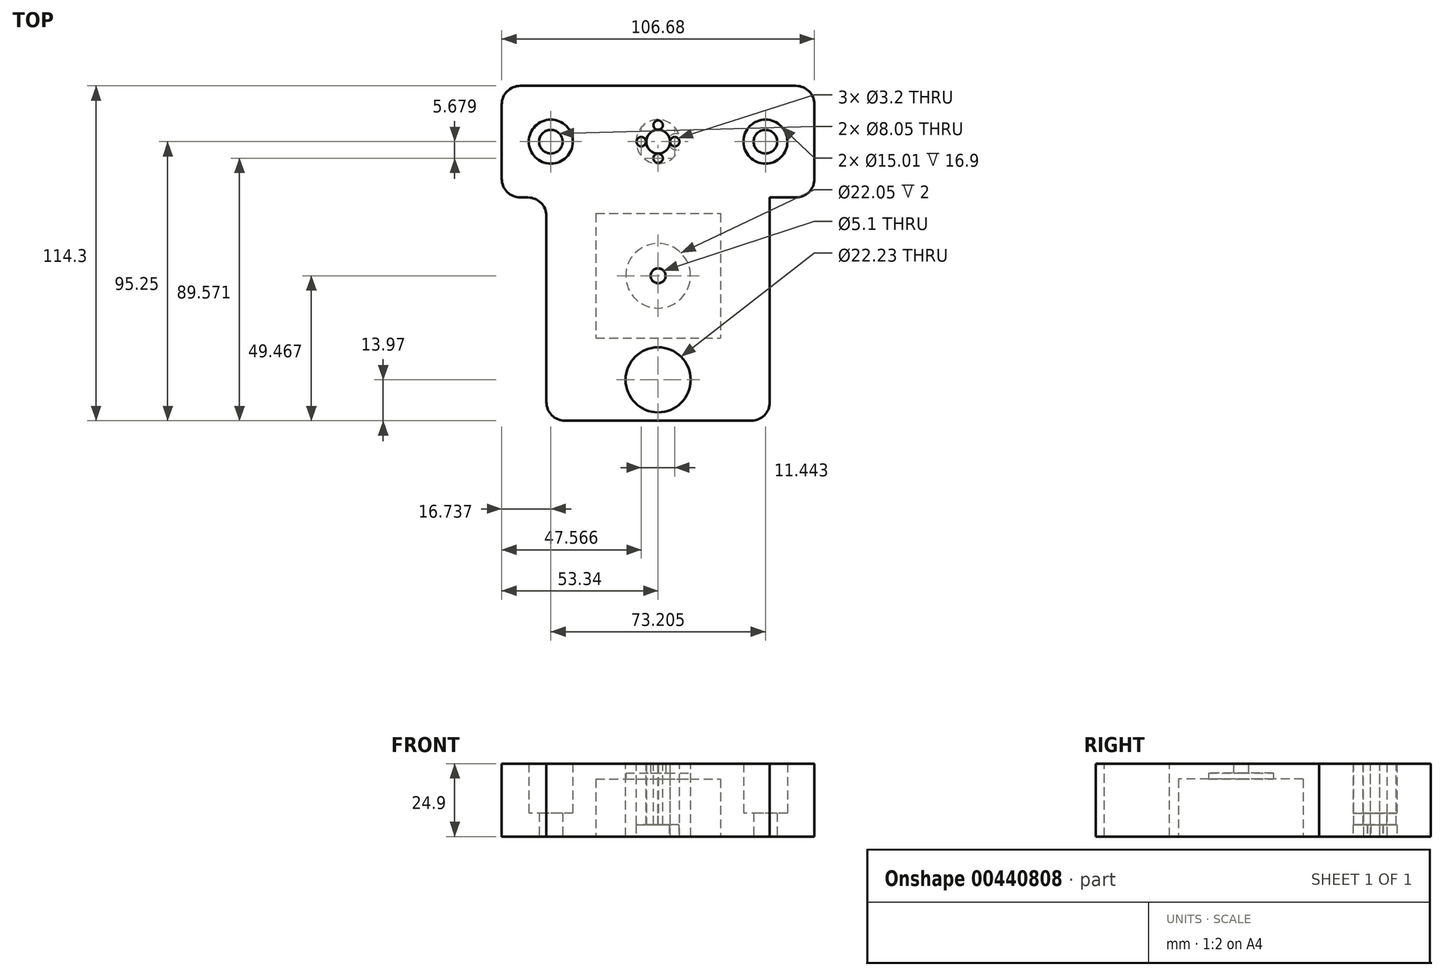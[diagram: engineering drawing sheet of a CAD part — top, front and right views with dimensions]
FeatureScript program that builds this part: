
annotation { "Feature Type Name" : "Feature", "Feature Type Description" : "" }
export const myFeature = defineFeature(function(context is Context, id is Id, definition is map)
    precondition{}
    {
        {
            var Q0;
            Q0=qCreatedBy(makeId("Top.planeOp"),FACE);
            var sketch = newSketch(context, id + "F0", { "sketchPlane" : qUnion([Q0])});
            skLineSegment(sketch, "E0.bottom", {"start": v(53.34, 19.05) * mm, "end": v(-53.34, 19.05) * mm});
            skLineSegment(sketch, "E0.top", {"start": v(53.34, -19.05) * mm, "end": v(-53.34, -19.05) * mm});
            skLineSegment(sketch, "E0.left", {"start": v(53.34, 19.05) * mm, "end": v(53.34, -19.05) * mm});
            skLineSegment(sketch, "E0.right", {"start": v(-53.34, 19.05) * mm, "end": v(-53.34, -19.05) * mm});
            skPoint(sketch, "E0.middle", {"position": v(0, 0) * mm});
            skCircle(sketch, "E1", {"center": v(-36.6, 0) * mm, "radius": 4.03 * mm});
            skCircle(sketch, "E2.MirrorC", {"center": v(36.6, 0) * mm, "radius": 4.03 * mm});
            skCircle(sketch, "E3", {"center": v(0, 0) * mm, "radius": 4.05 * mm});
            skSolve(sketch);
        }
        {
            var Q0;
            Q0=makeQuery(id+"F0.imprint","IMPRINT",FACE,{"disambiguationData":[TD([[makeQuery(id+"F0.imprint","IMPRINT",EDGE,{"derivedFrom":sQuery(id+"F0.wireOp",EDGE,"E0.bottom")}),1.0]])]});
            extrude(context, id + "F1", {"entities" : qUnion([Q0]), "depth" : 8 * mm});
        }
        {
            var Q0;
            Q0=makeQuery(id+"F1.opExtrude","CAP_FACE",FACE,{"disambiguationData":[OSD([sQuery(id+"F0.wireOp",EDGE,"E0.bottom"),sQuery(id+"F0.wireOp",EDGE,"E0.top"),sQuery(id+"F0.wireOp",EDGE,"E0.left"),sQuery(id+"F0.wireOp",EDGE,"E0.right"),sQuery(id+"F0.wireOp",EDGE,"E1"),sQuery(id+"F0.wireOp",EDGE,"E2.MirrorC"),sQuery(id+"F0.wireOp",EDGE,"E3")])],"isStart":true});
            var sketch = newSketch(context, id + "F2", { "sketchPlane" : qUnion([Q0])});
            skCircle(sketch, "E4", {"center": v(0, 0) * mm, "radius": 7.5 * mm});
            skCircle(sketch, "E5", {"center": v(0, 6.14) * mm, "radius": 2.75 * mm});
            skCircle(sketch, "E6", {"center": v(6.13, 0) * mm, "radius": 2.75 * mm});
            skCircle(sketch, "E7", {"center": v(0, -6.01) * mm, "radius": 2.75 * mm});
            skCircle(sketch, "E8", {"center": v(-6.08, 0) * mm, "radius": 2.75 * mm});
            skSolve(sketch);
        }
        {
            var Q0;
            {var subQ0=sQuery(id+"F2.wireOp",EDGE,"E5");var subQ1=sQuery(id+"F2.wireOp",EDGE,"E4");var subQ2=makeQuery(id+"F2.imprint","INTERSECT",VERTEX,{"disambiguationData":[OD(0.0)],"derivedFrom":[subQ1,subQ0]});Q0=makeQuery(id+"F2.imprint","IMPRINT",FACE,{"disambiguationData":[TD([[makeQuery(id+"F2.imprint","IMPRINT",EDGE,{"disambiguationData":[TD([[subQ2,-1.0]])],"derivedFrom":subQ1}),1.0]])]});}
            var Q1;
            {var subQ0=sQuery(id+"F2.wireOp",EDGE,"E8");var subQ1=sQuery(id+"F2.wireOp",EDGE,"E4");var subQ2=makeQuery(id+"F2.imprint","INTERSECT",VERTEX,{"disambiguationData":[OD(0.0)],"derivedFrom":[subQ1,subQ0]});Q1=makeQuery(id+"F2.imprint","IMPRINT",FACE,{"disambiguationData":[TD([[makeQuery(id+"F2.imprint","IMPRINT",EDGE,{"disambiguationData":[TD([[subQ2,-1.0]])],"derivedFrom":subQ1}),1.0]])]});}
            var Q2;
            {var subQ0=sQuery(id+"F2.wireOp",EDGE,"E6");var subQ1=sQuery(id+"F2.wireOp",EDGE,"E4");var subQ2=makeQuery(id+"F2.imprint","INTERSECT",VERTEX,{"disambiguationData":[OD(0.0)],"derivedFrom":[subQ1,subQ0]});Q2=makeQuery(id+"F2.imprint","IMPRINT",FACE,{"disambiguationData":[TD([[makeQuery(id+"F2.imprint","IMPRINT",EDGE,{"disambiguationData":[TD([[subQ2,1.0]])],"derivedFrom":subQ1}),1.0]])]});}
            var Q3;
            {var subQ0=sQuery(id+"F2.wireOp",EDGE,"E7");var subQ1=sQuery(id+"F2.wireOp",EDGE,"E4");var subQ2=makeQuery(id+"F2.imprint","INTERSECT",VERTEX,{"disambiguationData":[OD(0.0)],"derivedFrom":[subQ1,subQ0]});Q3=makeQuery(id+"F2.imprint","IMPRINT",FACE,{"disambiguationData":[TD([[makeQuery(id+"F2.imprint","IMPRINT",EDGE,{"disambiguationData":[TD([[subQ2,-1.0]])],"derivedFrom":subQ1}),1.0]])]});}
            var Q4;
            {var subQ1=sQuery(id+"F2.wireOp",EDGE,"E4");var subQ11=sQuery(id+"F2.wireOp",EDGE,"E5");var subQ14=makeQuery(id+"F2.imprint","INTERSECT",VERTEX,{"disambiguationData":[OD(0.0)],"derivedFrom":[subQ1,subQ11]});Q4=makeQuery(id+"F2.imprint","IMPRINT",FACE,{"disambiguationData":[TD([[makeQuery(id+"F2.imprint","IMPRINT",EDGE,{"disambiguationData":[TD([[subQ14,1.0]])],"derivedFrom":subQ1}),1.0]])]});}
            var Q5;
            {var subQ0=sQuery(id+"F2.wireOp",EDGE,"E7");var subQ1=makeQuery(id+"F1.opExtrude","CAP_EDGE",EDGE,{"disambiguationData":[OSD([sQuery(id+"F0.wireOp",EDGE,"E3")])],"isStart":true});var subQ2=makeQuery(id+"F2.imprint","INTERSECT",VERTEX,{"disambiguationData":[OD(0.0)],"derivedFrom":[subQ1,subQ0]});Q5=makeQuery(id+"F2.imprint","IMPRINT",FACE,{"disambiguationData":[TD([[makeQuery(id+"F2.imprint","IMPRINT",EDGE,{"disambiguationData":[TD([[subQ2,1.0]])],"derivedFrom":subQ0}),1.0]])]});}
            var Q6;
            {var subQ0=sQuery(id+"F2.wireOp",EDGE,"E8");var subQ1=sQuery(id+"F2.wireOp",EDGE,"E4");var subQ2=makeQuery(id+"F2.imprint","INTERSECT",VERTEX,{"disambiguationData":[OD(1.0)],"derivedFrom":[subQ1,subQ0]});Q6=makeQuery(id+"F2.imprint","IMPRINT",FACE,{"disambiguationData":[TD([[makeQuery(id+"F2.imprint","IMPRINT",EDGE,{"disambiguationData":[TD([[subQ2,-1.0]])],"derivedFrom":subQ1}),1.0]])]});}
            var Q7;
            {var subQ0=sQuery(id+"F2.wireOp",EDGE,"E7");var subQ1=sQuery(id+"F2.wireOp",EDGE,"E4");var subQ2=makeQuery(id+"F2.imprint","INTERSECT",VERTEX,{"disambiguationData":[OD(1.0)],"derivedFrom":[subQ1,subQ0]});Q7=makeQuery(id+"F2.imprint","IMPRINT",FACE,{"disambiguationData":[TD([[makeQuery(id+"F2.imprint","IMPRINT",EDGE,{"disambiguationData":[TD([[subQ2,-1.0]])],"derivedFrom":subQ1}),1.0]])]});}
            var Q8;
            {var subQ0=sQuery(id+"F2.wireOp",EDGE,"E5");var subQ1=sQuery(id+"F2.wireOp",EDGE,"E4");var subQ2=makeQuery(id+"F2.imprint","INTERSECT",VERTEX,{"disambiguationData":[OD(1.0)],"derivedFrom":[subQ1,subQ0]});Q8=makeQuery(id+"F2.imprint","IMPRINT",FACE,{"disambiguationData":[TD([[makeQuery(id+"F2.imprint","IMPRINT",EDGE,{"disambiguationData":[TD([[subQ2,-1.0]])],"derivedFrom":subQ1}),1.0]])]});}
            extrude(context, id + "F3", {"entities" : qUnion([Q0, Q1, Q2, Q3, Q4, Q5, Q6, Q7, Q8]), "operationType" : NewBodyOperationType.REMOVE, "oppositeDirection" : true, "depth" : 4.05 * mm});
        }
        {
            var Q0;
            Q0=makeQuery(id+"F1.opExtrude","CAP_FACE",FACE,{"disambiguationData":[OSD([sQuery(id+"F0.wireOp",EDGE,"E0.bottom"),sQuery(id+"F0.wireOp",EDGE,"E0.top"),sQuery(id+"F0.wireOp",EDGE,"E0.left"),sQuery(id+"F0.wireOp",EDGE,"E0.right"),sQuery(id+"F0.wireOp",EDGE,"E1"),sQuery(id+"F0.wireOp",EDGE,"E2.MirrorC"),sQuery(id+"F0.wireOp",EDGE,"E3")])],"isStart":false});
            var sketch = newSketch(context, id + "F4", { "sketchPlane" : qUnion([Q0])});
            skCircle(sketch, "E9", {"center": v(-5.77, 0) * mm, "radius": 1.6 * mm});
            skCircle(sketch, "E10", {"center": v(0, 5.65) * mm, "radius": 1.6 * mm});
            skCircle(sketch, "E11", {"center": v(5.67, 0) * mm, "radius": 1.6 * mm});
            skCircle(sketch, "E12", {"center": v(0, -5.68) * mm, "radius": 1.6 * mm});
            skSolve(sketch);
        }
        {
            var Q0;
            Q0 = qSketchRegion(id + "F4", true);
            extrude(context, id + "F5", {"entities" : qUnion([Q0]), "operationType" : NewBodyOperationType.REMOVE, "oppositeDirection" : true, "depth" : 25.4 * mm});
        }
        {
            var Q0;
            Q0=makeQuery(id+"F1.opExtrude","CAP_FACE",FACE,{"disambiguationData":[OSD([sQuery(id+"F0.wireOp",EDGE,"E0.bottom"),sQuery(id+"F0.wireOp",EDGE,"E0.top"),sQuery(id+"F0.wireOp",EDGE,"E0.left"),sQuery(id+"F0.wireOp",EDGE,"E0.right"),sQuery(id+"F0.wireOp",EDGE,"E1"),sQuery(id+"F0.wireOp",EDGE,"E2.MirrorC"),sQuery(id+"F0.wireOp",EDGE,"E3")])],"isStart":false});
            var sketch = newSketch(context, id + "F6", { "sketchPlane" : qUnion([Q0])});
            skCircle(sketch, "E13", {"center": v(-36.6, 0) * mm, "radius": 7.5 * mm});
            skCircle(sketch, "E14", {"center": v(36.6, 0) * mm, "radius": 7.5 * mm});
            skSolve(sketch);
        }
        {
            var Q0;
            Q0=makeQuery(id+"F6.imprint","IMPRINT",FACE,{"disambiguationData":[TD([[makeQuery(id+"F6.imprint","IMPRINT",EDGE,{"derivedFrom":sQuery(id+"F6.wireOp",EDGE,"E13")}),-1.0]])]});
            extrude(context, id + "F7", {"entities" : qUnion([Q0]), "operationType" : NewBodyOperationType.ADD, "depth" : 16.9 * mm});
        }
        {
            var Q0;
            Q0=makeQuery(id+"F7.opExtrude","CAP_FACE",FACE,{"disambiguationData":[OSD([sQuery(id+"F0.wireOp",EDGE,"E0.bottom"),sQuery(id+"F0.wireOp",EDGE,"E0.top"),sQuery(id+"F0.wireOp",EDGE,"E0.left"),sQuery(id+"F0.wireOp",EDGE,"E0.right"),sQuery(id+"F0.wireOp",EDGE,"E3"),sQuery(id+"F4.wireOp",EDGE,"E9"),sQuery(id+"F4.wireOp",EDGE,"E10"),sQuery(id+"F4.wireOp",EDGE,"E11"),sQuery(id+"F4.wireOp",EDGE,"E12"),sQuery(id+"F6.wireOp",EDGE,"E13"),sQuery(id+"F6.wireOp",EDGE,"E14")])],"isStart":false});
            var sketch = newSketch(context, id + "F8", { "sketchPlane" : qUnion([Q0])});
            skLineSegment(sketch, "E15", {"start": v(0, -19.05) * mm, "end": v(-38.1, -19.05) * mm});
            skLineSegment(sketch, "E16", {"start": v(0, -19.05) * mm, "end": v(38.1, -19.05) * mm});
            skLineSegment(sketch, "E17.bottom", {"start": v(-38.1, -19.05) * mm, "end": v(38.1, -19.05) * mm});
            skLineSegment(sketch, "E17.top", {"start": v(-38.1, -95.25) * mm, "end": v(38.1, -95.25) * mm});
            skLineSegment(sketch, "E17.left", {"start": v(-38.1, -19.05) * mm, "end": v(-38.1, -95.25) * mm});
            skLineSegment(sketch, "E17.right", {"start": v(38.1, -19.05) * mm, "end": v(38.1, -95.25) * mm});
            skSolve(sketch);
        }
        {
            var Q0;
            Q0 = qSketchRegion(id + "F8", true);
            extrude(context, id + "F9", {"entities" : qUnion([Q0]), "operationType" : NewBodyOperationType.ADD, "oppositeDirection" : true, "depth" : 24.9 * mm});
        }
        {
            var Q0;
            {var subQ0=sQuery(id+"F0.wireOp",EDGE,"E0.right");var subQ1=sQuery(id+"F0.wireOp",EDGE,"E0.top");Q0=makeQuery(id+"F7.boolean.opBoolean","MERGE",EDGE,{"derivedFrom":[makeQuery(id+"F1.opExtrude","SWEPT_EDGE",EDGE,{"disambiguationData":[OSD([subQ1,subQ0])]}),makeQuery(id+"F7.opExtrude","SWEPT_EDGE",EDGE,{"disambiguationData":[OSD([subQ1,subQ0])]})]});}
            var Q1;
            {var subQ0=sQuery(id+"F0.wireOp",EDGE,"E0.right");var subQ1=sQuery(id+"F0.wireOp",EDGE,"E0.bottom");Q1=makeQuery(id+"F7.boolean.opBoolean","MERGE",EDGE,{"derivedFrom":[makeQuery(id+"F1.opExtrude","SWEPT_EDGE",EDGE,{"disambiguationData":[OSD([subQ1,subQ0])]}),makeQuery(id+"F7.opExtrude","SWEPT_EDGE",EDGE,{"disambiguationData":[OSD([subQ1,subQ0])]})]});}
            var Q2;
            Q2=makeQuery(id+"F9.opExtrude","SWEPT_EDGE",EDGE,{"disambiguationData":[OSD([sQuery(id+"F8.wireOp",EDGE,"E17.top"),sQuery(id+"F8.wireOp",EDGE,"E17.left")])]});
            var Q3;
            {var subQ0=sQuery(id+"F0.wireOp",EDGE,"E0.left");var subQ1=sQuery(id+"F0.wireOp",EDGE,"E0.bottom");Q3=makeQuery(id+"F7.boolean.opBoolean","MERGE",EDGE,{"derivedFrom":[makeQuery(id+"F1.opExtrude","SWEPT_EDGE",EDGE,{"disambiguationData":[OSD([subQ1,subQ0])]}),makeQuery(id+"F7.opExtrude","SWEPT_EDGE",EDGE,{"disambiguationData":[OSD([subQ1,subQ0])]})]});}
            var Q4;
            {var subQ0=sQuery(id+"F0.wireOp",EDGE,"E0.left");var subQ1=sQuery(id+"F0.wireOp",EDGE,"E0.top");Q4=makeQuery(id+"F7.boolean.opBoolean","MERGE",EDGE,{"derivedFrom":[makeQuery(id+"F1.opExtrude","SWEPT_EDGE",EDGE,{"disambiguationData":[OSD([subQ1,subQ0])]}),makeQuery(id+"F7.opExtrude","SWEPT_EDGE",EDGE,{"disambiguationData":[OSD([subQ1,subQ0])]})]});}
            var Q5;
            Q5=makeQuery(id+"F9.opExtrude","SWEPT_EDGE",EDGE,{"disambiguationData":[OSD([sQuery(id+"F8.wireOp",EDGE,"E17.top"),sQuery(id+"F8.wireOp",EDGE,"E17.right")])]});
            var Q6;
            Q6=makeQuery(id+"F9.opExtrude","SWEPT_EDGE",EDGE,{"disambiguationData":[OSD([sQuery(id+"F0.wireOp",EDGE,"E0.top"),sQuery(id+"F8.wireOp",EDGE,"E17.bottom"),sQuery(id+"F8.wireOp",EDGE,"E17.right")])]});
            var Q7;
            Q7=makeQuery(id+"F9.opExtrude","SWEPT_EDGE",EDGE,{"disambiguationData":[OSD([sQuery(id+"F0.wireOp",EDGE,"E0.top"),sQuery(id+"F8.wireOp",EDGE,"E17.bottom"),sQuery(id+"F8.wireOp",EDGE,"E17.left")])]});
            fillet(context, id + "F10", {"entities" : qUnion([Q0, Q1, Q2, Q3, Q4, Q5, Q6, Q7]), "radius" : 6.35 * mm, "tangentPropagation" : true, "allowEdgeOverflow" : false});
        }
        {
            var Q0;
            Q0=makeQuery(id+"F9.opExtrude","CAP_FACE",FACE,{"disambiguationData":[OSD([sQuery(id+"F8.wireOp",EDGE,"E17.bottom"),sQuery(id+"F8.wireOp",EDGE,"E17.top"),sQuery(id+"F8.wireOp",EDGE,"E17.left"),sQuery(id+"F8.wireOp",EDGE,"E17.right")])],"isStart":false});
            var sketch = newSketch(context, id + "F11", { "sketchPlane" : qUnion([Q0])});
            skLineSegment(sketch, "E18", {"start": v(-38.1, 19.05) * mm, "end": v(-21.25, 19.05) * mm});
            skLineSegment(sketch, "E19", {"start": v(-21.25, 19.05) * mm, "end": v(-21.25, 24.53) * mm});
            skLineSegment(sketch, "E20.bottom", {"start": v(-21.25, 24.53) * mm, "end": v(21.25, 24.53) * mm});
            skLineSegment(sketch, "E20.top", {"start": v(-21.25, 67.03) * mm, "end": v(21.25, 67.03) * mm});
            skLineSegment(sketch, "E20.left", {"start": v(-21.25, 24.53) * mm, "end": v(-21.25, 67.03) * mm});
            skLineSegment(sketch, "E20.right", {"start": v(21.25, 24.53) * mm, "end": v(21.25, 67.03) * mm});
            skPoint(sketch, "E21.62.internal.snap0", {"position": v(39.96, 20.9) * mm});
            skPoint(sketch, "E21.63.internal.snap0", {"position": v(39.96, 20.9) * mm});
            skPoint(sketch, "E21.65.internal.snap0", {"position": v(39.96, 20.9) * mm});
            skSolve(sketch);
        }
        {
            var Q0;
            Q0 = qSketchRegion(id + "F11", true);
            extrude(context, id + "F12", {"entities" : qUnion([Q0]), "operationType" : NewBodyOperationType.REMOVE, "oppositeDirection" : true, "depth" : 19.63 * mm});
        }
        {
            var Q0;
            Q0=makeQuery(id+"F12.boolean.opBoolean","COPY",FACE,{"derivedFrom":makeQuery(id+"F12.opExtrude","CAP_FACE",FACE,{"disambiguationData":[OSD([sQuery(id+"F11.wireOp",EDGE,"E20.bottom"),sQuery(id+"F11.wireOp",EDGE,"E20.top"),sQuery(id+"F11.wireOp",EDGE,"E20.left"),sQuery(id+"F11.wireOp",EDGE,"E20.right")])],"isStart":false})});
            var sketch = newSketch(context, id + "F13", { "sketchPlane" : qUnion([Q0])});
            skLineSegment(sketch, "E22", {"start": v(0, 24.53) * mm, "end": v(0, 67.03) * mm});
            skCircle(sketch, "E23", {"center": v(0, 45.78) * mm, "radius": 11.03 * mm});
            skSolve(sketch);
        }
        {
            var Q0;
            Q0 = qSketchRegion(id + "F13", true);
            extrude(context, id + "F14", {"entities" : qUnion([Q0]), "operationType" : NewBodyOperationType.REMOVE, "oppositeDirection" : true, "depth" : 2 * mm});
        }
        {
            var Q0;
            Q0=makeQuery(id+"F14.boolean.opBoolean","COPY",FACE,{"derivedFrom":makeQuery(id+"F14.opExtrude","CAP_FACE",FACE,{"disambiguationData":[OSD([sQuery(id+"F13.wireOp",EDGE,"E23")])],"isStart":false})});
            var sketch = newSketch(context, id + "F15", { "sketchPlane" : qUnion([Q0])});
            skCircle(sketch, "E24", {"center": v(0, 45.78) * mm, "radius": 2.55 * mm});
            skSolve(sketch);
        }
        {
            var Q0;
            Q0=makeQuery(id+"F15.imprint","IMPRINT",FACE,{"disambiguationData":[TD([[makeQuery(id+"F15.imprint","IMPRINT",EDGE,{"derivedFrom":sQuery(id+"F15.wireOp",EDGE,"E24")}),1.0]])]});
            extrude(context, id + "F16", {"entities" : qUnion([Q0]), "operationType" : NewBodyOperationType.REMOVE, "oppositeDirection" : true, "depth" : 25.4 * mm});
        }
        {
            var Q0;
            Q0=makeQuery(id+"F9.boolean.opBoolean","MERGE",FACE,{"derivedFrom":[makeQuery(id+"F7.opExtrude","CAP_FACE",FACE,{"disambiguationData":[OSD([sQuery(id+"F0.wireOp",EDGE,"E0.bottom"),sQuery(id+"F0.wireOp",EDGE,"E0.top"),sQuery(id+"F0.wireOp",EDGE,"E0.left"),sQuery(id+"F0.wireOp",EDGE,"E0.right"),sQuery(id+"F0.wireOp",EDGE,"E3"),sQuery(id+"F4.wireOp",EDGE,"E9"),sQuery(id+"F4.wireOp",EDGE,"E10"),sQuery(id+"F4.wireOp",EDGE,"E11"),sQuery(id+"F4.wireOp",EDGE,"E12"),sQuery(id+"F6.wireOp",EDGE,"E13"),sQuery(id+"F6.wireOp",EDGE,"E14")])],"isStart":false}),makeQuery(id+"F9.opExtrude","CAP_FACE",FACE,{"disambiguationData":[OSD([sQuery(id+"F8.wireOp",EDGE,"E17.bottom"),sQuery(id+"F8.wireOp",EDGE,"E17.top"),sQuery(id+"F8.wireOp",EDGE,"E17.left"),sQuery(id+"F8.wireOp",EDGE,"E17.right")])],"isStart":true})]});
            var sketch = newSketch(context, id + "F17", { "sketchPlane" : qUnion([Q0])});
            skLineSegment(sketch, "E25", {"start": v(0, -95.25) * mm, "end": v(0, -81.28) * mm});
            skPoint(sketch, "E25.endSnap0", {"position": v(0, -95.25) * mm});
            skCircle(sketch, "E26", {"center": v(0, -81.28) * mm, "radius": 11.11 * mm});
            skSolve(sketch);
        }
        {
            var Q0;
            Q0 = qSketchRegion(id + "F17", true);
            extrude(context, id + "F18", {"entities" : qUnion([Q0]), "operationType" : NewBodyOperationType.REMOVE, "oppositeDirection" : true, "depth" : 25.4 * mm});
        }
    });
